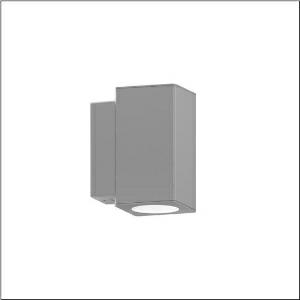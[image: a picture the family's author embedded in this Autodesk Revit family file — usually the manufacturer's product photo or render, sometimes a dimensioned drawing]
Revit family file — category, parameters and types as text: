
# Revit family: cl_31_wand_5cl563623
name_source: partatom
category: Lighting Fixtures
units: mm (PartAtom-declared; Revit-internal decimal feet)

## family parameters
Cut with Voids When Loaded = No
Host = Face
Light Source = No
Part Type = Normal
Room Calculation Point = No
Round Connector Dimension = Use Diameter
Shared = No

## types (1)
- --- (1 x LED, 600 lm, 5.4 W, 3000K)
    Apparent Load = 5 VA
    CIE Flux Codes = 98 100 100 50 100
    Color Rendering = 80
    Color Temperature = 3000K
    Default Elevation = 1800 mm
    Description = CL 31 Wall, wall luminaire, primary light control with reflector, of aluminium, primary optical cover: cover panel, of glass, transparent, light emission: up/down distribution, primary light characteristic: symmetric, installation type: surface-mounted, for 2x LED, rated luminous flux: 300lm, luminous efficacy: 110lm/W, light colour: 830, colour temperature: 3000K, control gear: DALI, with terminal, 5-pole, max. 2.5mm², mains connection: 220..240V, AC, 50/60Hz, rated input power: 5.5W, luminaire housing, square, of aluminium, powder-coated, Siteco® metallic grey, length: 143mm, width: 100mm, height: 186mm, protection rating (complete): IP65, insulation class (complete): insulation class I (protective earthing), certification: CE, ENEC, impact resistance: IK08, permissible operating ambient temperature for outdoor applications: -20..+50°C, packaging unit: 1 piece
    Height = 186 mm
    Lamp = 1 x LED
    Lamp Light Flux = 600 lm
    Lamp Power = 5.4 W
    Lamp count = 1
    Length = 100 mm  [stored 0.328084 ft]
    Luminous efficacy = 111 lm/W
    Manufacturer = Siteco
    ModVariant = No
    Model = 5CL563623
    Mounting Place = Wall
    Mounting Type = Surface mounted
    Number of Poles = 1
    OnlyDefault = Yes
    Power Factor = 1
    Product Name = CL 31 Wand
    Product group = wall luminaire
    ProductGroupID = 2002
    Protection Class = Protection class I
    Protection Degree = IP 65
    RLX_Detail_Level = 1
    RLX_Emergency_Light_Flux = 0 lm
    RLX_Emergency_Type = 0
    RLX_Emergency_Type_DB = No
    RlxData = <blob elided: 40449 chars, md5=5e4d1a97>
    Socket = socket
    Standby Power = 0 W
    System Light Flux = 600 lm
    System Power = 5 W
    Type Comments = factory setting: luminous flux: 100 % | dim-lin: 254 | 135 mA
    Type Image = l_1006895.jpg
    URL = http://relux.com
    VarID = @adj_216721
    Voltage = 0 V
    Weight = 0.00 kg
    Width = 143 mm

note: [stored X ft] marks values corroborated as IEEE doubles in the binary element streams (Revit-internal decimal feet)

## geometry (parser evidence)
native form markers: Blend x4, Sweep x11
no freeform markers — native parametric forms only
